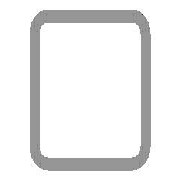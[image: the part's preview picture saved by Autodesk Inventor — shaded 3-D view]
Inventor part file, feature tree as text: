
AUTODESK INVENTOR PART (.ipt)
format: ipt  version: 2024.2 (Build 282272000, 272)  size: 145,920 bytes
history: native  units: mm (DEFAULTED — no unit token found)
features: other x4, sketch x2, extrude x1, plane x1, projected_geometry x1
ambient origin geometry x8: Origin, YZ Plane, XZ Plane, XY Plane, X Axis, Y Axis, Z Axis, Center Point
bodies: Solid1 (feature_tree), Body (feature_tree)
feature tree (9):
  parser-record x1  (decoder bookkeeping rows leaked as tree rows — omitted from the tree; the rows remain in map.json)
  other  "Driven Length"
  other  "Start Plane"
  other  "End Plane"
  extrude  "Extrusion2"  TaperAngle=0.0deg  [1 undecoded]
  sketch  "Sketch3"  dims[d3=700.0mm d4=0.0mm]
  plane  "Work Plane3"
  sketch  "Sketch5"  dims[d7=4.0mm d9=40.0mm d11=40.0mm d12=2.0mm d13=-0.0mm d14=700.0mm d15=20.0mm d16=20.0mm d17=90.0deg d18=700.0mm d19=11.0mm d20=40.0mm d21=200.0mm d22=10.0mm d23=0.0mm]
  projected_geometry  "Projected Loop1"
note: 1 required parameter value undecoded (feature->parameter linkage not recoverable at this tier; creation-order binding heuristic only, values carry confidence <= 0.55)
